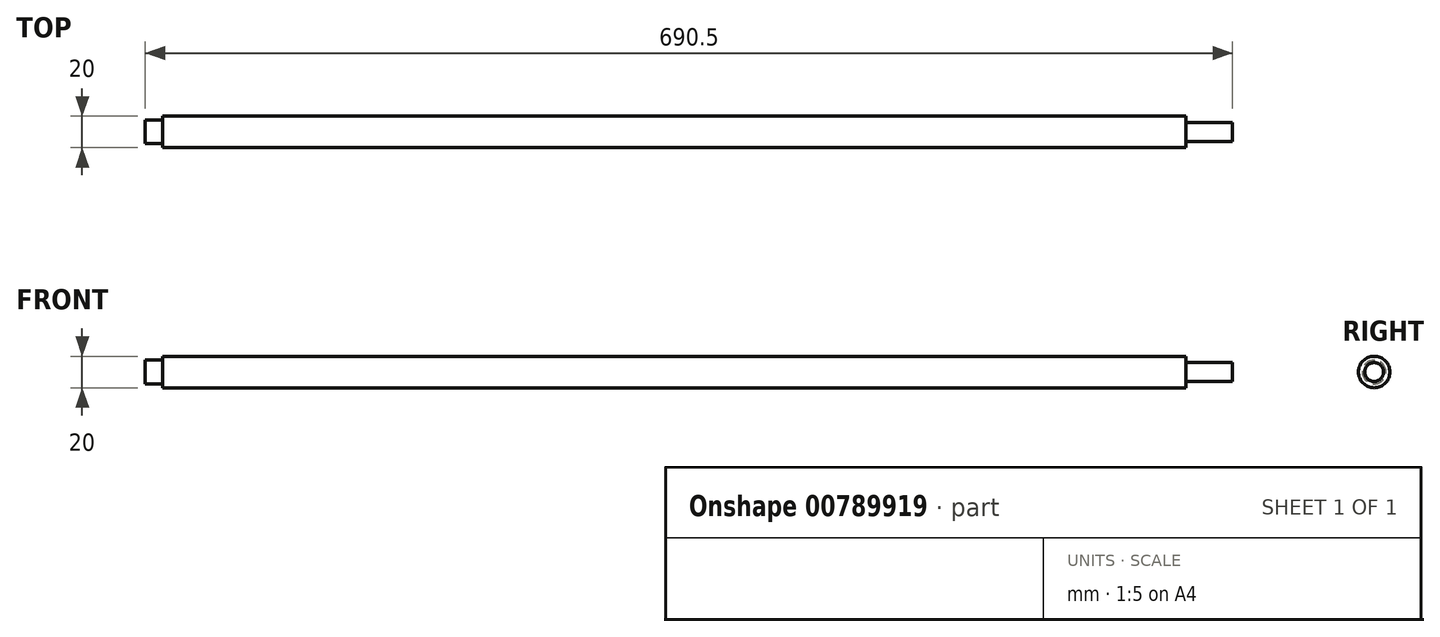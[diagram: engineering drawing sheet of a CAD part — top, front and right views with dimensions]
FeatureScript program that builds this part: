
annotation { "Feature Type Name" : "Feature", "Feature Type Description" : "" }
export const myFeature = defineFeature(function(context is Context, id is Id, definition is map)
    precondition{}
    {
        {
            var Q0;
            Q0=qCreatedBy(makeId("Right.planeOp"),FACE);
            var sketch = newSketch(context, id + "F0", { "sketchPlane" : qUnion([Q0])});
            skCircle(sketch, "E0", {"center": v(0, 0) * mm, "radius": 10 * mm});
            skSolve(sketch);
        }
        {
            var Q0;
            Q0=makeQuery(id+"F0.imprint","IMPRINT",FACE,{"disambiguationData":[TD([[makeQuery(id+"F0.imprint","IMPRINT",EDGE,{"derivedFrom":sQuery(id+"F0.wireOp",EDGE,"E0")}),1.0]])]});
            extrude(context, id + "F1", {"entities" : qUnion([Q0]), "depth" : 650 * mm, "offsetDistance" : 25 * mm, "symmetric" : true});
        }
        {
            var Q0;
            Q0=makeQuery(id+"F1.opExtrude","CAP_FACE",FACE,{"disambiguationData":[OSD([sQuery(id+"F0.wireOp",EDGE,"E0")])],"isStart":true});
            var sketch = newSketch(context, id + "F2", { "sketchPlane" : qUnion([Q0])});
            skCircle(sketch, "E1", {"center": v(0, 0) * mm, "radius": 7.5 * mm});
            skSolve(sketch);
        }
        {
            var Q0;
            Q0=qSketchRegion(id+"F2",true);
            extrude(context, id + "F3", {"entities" : qUnion([Q0]), "operationType" : NewBodyOperationType.ADD, "depth" : 11 * mm, "offsetDistance" : 25 * mm});
        }
        {
            var Q0;
            Q0=makeQuery(id+"F1.opExtrude","CAP_FACE",FACE,{"disambiguationData":[OSD([sQuery(id+"F0.wireOp",EDGE,"E0")])],"isStart":false});
            var sketch = newSketch(context, id + "F4", { "sketchPlane" : qUnion([Q0])});
            skCircle(sketch, "E2", {"center": v(0, 0) * mm, "radius": 6 * mm});
            skSolve(sketch);
        }
        {
            var Q0;
            Q0=makeQuery(id+"F4.imprint","IMPRINT",FACE,{"disambiguationData":[TD([[makeQuery(id+"F4.imprint","IMPRINT",EDGE,{"derivedFrom":sQuery(id+"F4.wireOp",EDGE,"E2")}),1.0]])]});
            extrude(context, id + "F5", {"entities" : qUnion([Q0]), "operationType" : NewBodyOperationType.ADD, "depth" : 29.5 * mm, "offsetDistance" : 25 * mm});
        }
    });
